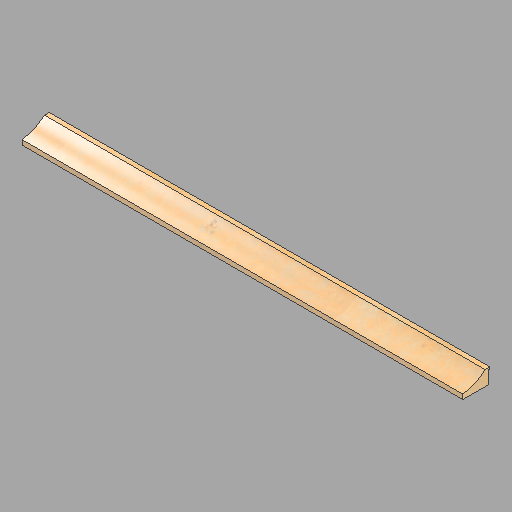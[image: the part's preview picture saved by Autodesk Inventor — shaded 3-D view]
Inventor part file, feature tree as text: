
AUTODESK INVENTOR PART (.ipt)
format: ipt  version: 2022.2 (Build 262287010, 287A)  size: 165,376 bytes
history: native  units: in
note: dims shown in document units (in); Inventor stores cm internally (conversion verified against a paired STEP export)
features: revolve x2, other x1, direct_edit x1
ambient origin geometry x8: Origin, YZ Plane, XZ Plane, XY Plane, X Axis, Y Axis, Z Axis, Center Point
bodies: Solid1 (feature_tree)
feature tree (4):
  other  "Jamb (Lower)"
  direct_edit  "Direct Edit2"
  revolve  "Rotate3"  [1 undecoded]
  revolve  "Rotate4"  [1 undecoded]
note: 2 required parameter values undecoded (feature->parameter linkage not recoverable at this tier; creation-order binding heuristic only, values carry confidence <= 0.55)
